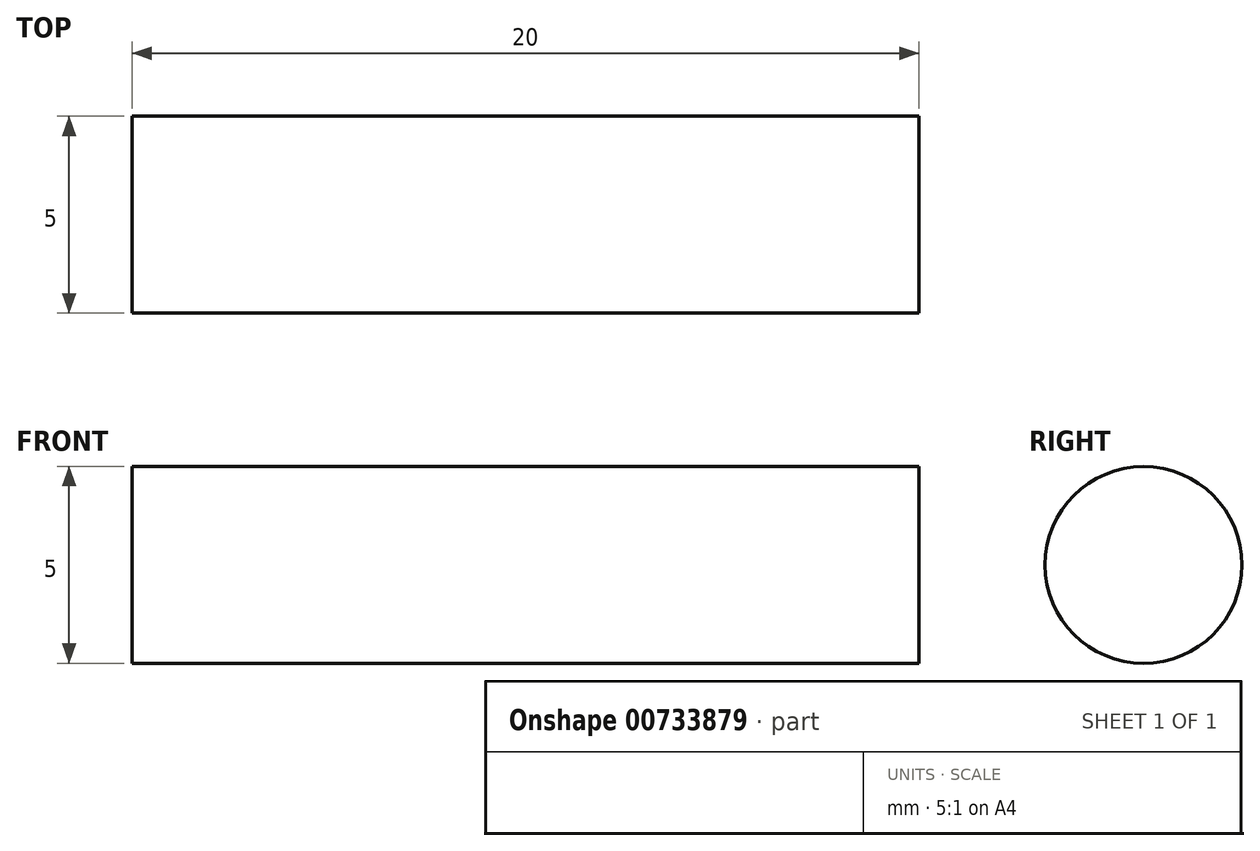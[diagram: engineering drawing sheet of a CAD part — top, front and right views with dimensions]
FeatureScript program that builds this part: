
annotation { "Feature Type Name" : "Feature", "Feature Type Description" : "" }
export const myFeature = defineFeature(function(context is Context, id is Id, definition is map)
    precondition{}
    {
        {
            var Q0;
            Q0=qCreatedBy(makeId("Right.planeOp"),FACE);
            var sketch = newSketch(context, id + "F0", { "sketchPlane" : qUnion([Q0])});
            skCircle(sketch, "E0", {"center": v(0, 0) * mm, "radius": 2.5 * mm});
            skSolve(sketch);
        }
        {
            var Q0;
            Q0=makeQuery(id+"F0.imprint","IMPRINT",FACE,{"disambiguationData":[TD([[makeQuery(id+"F0.imprint","IMPRINT",EDGE,{"derivedFrom":sQuery(id+"F0.wireOp",EDGE,"E0")}),1.0]])]});
            extrude(context, id + "F1", {"entities" : qUnion([Q0]), "depth" : 20 * mm, "offsetDistance" : 25 * mm});
        }
    });
